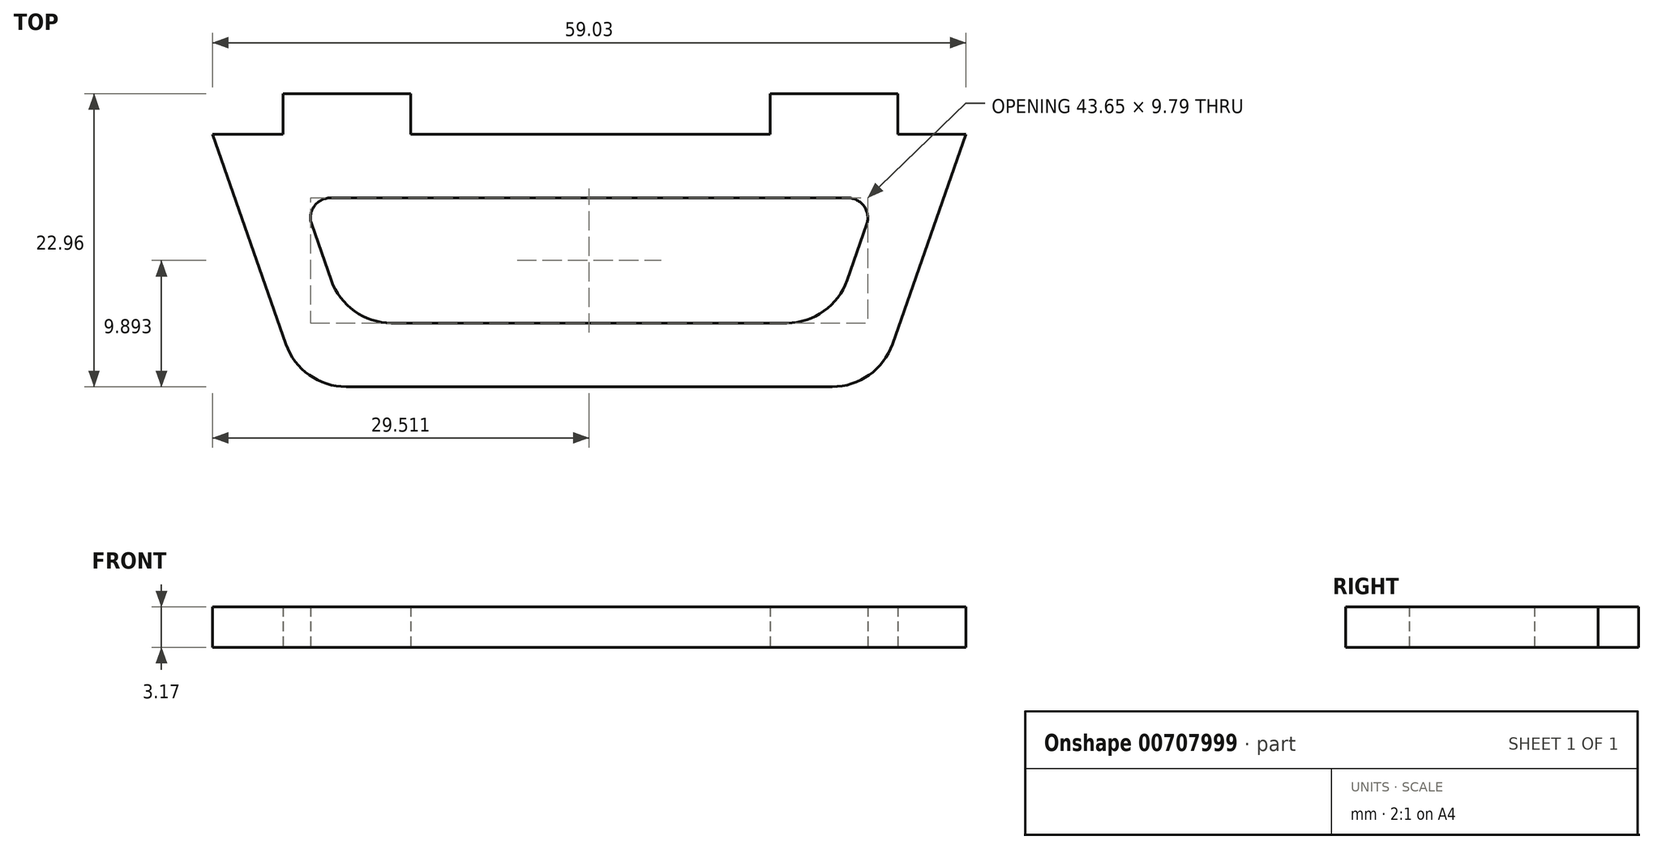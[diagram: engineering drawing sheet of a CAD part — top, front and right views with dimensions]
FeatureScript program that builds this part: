
annotation { "Feature Type Name" : "Feature", "Feature Type Description" : "" }
export const myFeature = defineFeature(function(context is Context, id is Id, definition is map)
    precondition{}
    {
        {
            var Q0;
            Q0=qCreatedBy(makeId("Top.planeOp"), FACE);
            var sketch = newSketch(context, id + "F0", { "sketchPlane" : qUnion([Q0])});
            skPoint(sketch, "E0.0", {"position": v(-32.01, 51.6) * mm});
            skPoint(sketch, "E1.0", {"position": v(27.02, 51.6) * mm});
            skLineSegment(sketch, "E2.0", {"start": v(21.69, 4.24) * mm, "end": v(27.02, 4.24) * mm});
            skPoint(sketch, "E3.0", {"position": v(2.5, 5.83) * mm});
            skPoint(sketch, "E4.0", {"position": v(-5, 7.41) * mm});
            skPoint(sketch, "E5.0", {"position": v(-7.5, 5.83) * mm});
            skLineSegment(sketch, "E6.0", {"start": v(-32.01, 4.24) * mm, "end": v(-26.5, 4.24) * mm});
            skLineSegment(sketch, "E7", {"start": v(27.02, 51.6) * mm, "end": v(27.02, 4.24) * mm, "construction": true});
            skLineSegment(sketch, "E8", {"start": v(-32.01, 51.6) * mm, "end": v(-32.01, 4.24) * mm, "construction": true});
            skLineSegment(sketch, "E9", {"start": v(27.02, 4.24) * mm, "end": v(21.26, -12.2) * mm});
            skLineSegment(sketch, "E10", {"start": v(-2.5, 7.41) * mm, "end": v(-2.5, -4.65) * mm, "construction": true});
            skLineSegment(sketch, "E11.MirrorCS", {"start": v(-32.01, 4.24) * mm, "end": v(-26.26, -12.2) * mm});
            skLineSegment(sketch, "E12", {"start": v(16.54, -15.55) * mm, "end": v(-21.54, -15.55) * mm});
            skPoint(sketch, "E13.orphan", {"position": v(30.38, 4.24) * mm});
            skPoint(sketch, "E14.0.end.orphan", {"position": v(24.6, -12.28) * mm});
            skPoint(sketch, "E15.visualSharp", {"position": v(20.08, -15.55) * mm});
            skArc(sketch, "E15.filletArc", {"start": v(16.54, -15.55) * mm, "mid": v(19.43, -14.63) * mm, "end": v(21.26, -12.2) * mm});
            skPoint(sketch, "E16.visualSharp", {"position": v(-25.08, -15.55) * mm});
            skArc(sketch, "E16.filletArc", {"start": v(-26.26, -12.2) * mm, "mid": v(-24.43, -14.63) * mm, "end": v(-21.54, -15.55) * mm});
            skLineSegment(sketch, "E17", {"start": v(13, -10.55) * mm, "end": v(-17.99, -10.55) * mm});
            skLineSegment(sketch, "E18.0", {"start": v(2.5, -0.76) * mm, "end": v(17.78, -0.76) * mm});
            skLineSegment(sketch, "E19.0", {"start": v(-7.5, -0.76) * mm, "end": v(2.5, -0.76) * mm});
            skLineSegment(sketch, "E20.0", {"start": v(-22.78, -0.76) * mm, "end": v(-7.5, -0.76) * mm});
            skPoint(sketch, "E21.orphan", {"position": v(20.6, -0.76) * mm});
            skLineSegment(sketch, "E22.trimOffspring", {"start": v(19.24, -2.83) * mm, "end": v(17.71, -7.2) * mm});
            skPoint(sketch, "E23.orphan", {"position": v(-25.59, -0.76) * mm});
            skLineSegment(sketch, "E24.trimOffspring", {"start": v(-24.24, -2.83) * mm, "end": v(-22.7, -7.2) * mm});
            skArc(sketch, "E25.filletArc", {"start": v(13, -10.55) * mm, "mid": v(15.88, -9.63) * mm, "end": v(17.71, -7.2) * mm});
            skArc(sketch, "E26.filletArc", {"start": v(-22.7, -7.2) * mm, "mid": v(-20.88, -9.63) * mm, "end": v(-17.99, -10.55) * mm});
            skPoint(sketch, "E27.visualSharp", {"position": v(-24.96, -0.76) * mm});
            skArc(sketch, "E27.filletArc", {"start": v(-22.78, -0.76) * mm, "mid": v(-24.04, -1.42) * mm, "end": v(-24.24, -2.83) * mm});
            skPoint(sketch, "E28.visualSharp", {"position": v(19.97, -0.76) * mm});
            skArc(sketch, "E28.filletArc", {"start": v(19.24, -2.83) * mm, "mid": v(19.05, -1.42) * mm, "end": v(17.78, -0.76) * mm});
            skPoint(sketch, "E29.orphan", {"position": v(-35.37, 4.24) * mm});
            skLineSegment(sketch, "E30", {"start": v(21.69, 4.24) * mm, "end": v(21.69, 7.41) * mm});
            skLineSegment(sketch, "E31", {"start": v(21.69, 7.41) * mm, "end": v(11.69, 7.41) * mm});
            skLineSegment(sketch, "E32", {"start": v(-16.5, 7.41) * mm, "end": v(-26.5, 7.41) * mm});
            skLineSegment(sketch, "E33", {"start": v(-26.5, 7.41) * mm, "end": v(-26.5, 4.24) * mm});
            skLineSegment(sketch, "E34", {"start": v(-16.5, 7.41) * mm, "end": v(-16.5, 4.24) * mm});
            skLineSegment(sketch, "E35", {"start": v(11.69, 7.41) * mm, "end": v(11.69, 4.24) * mm});
            skLineSegment(sketch, "E36", {"start": v(-16.5, 4.24) * mm, "end": v(11.69, 4.24) * mm});
            skSolve(sketch);
        }
        {
            var Q0;
            Q0 = qSketchRegion(id + "F0", true);
            extrude(context, id + "F1", {"entities" : qUnion([Q0]), "depth" : 3.17 * mm, "offsetDistance" : 25 * mm});
        }
    });
